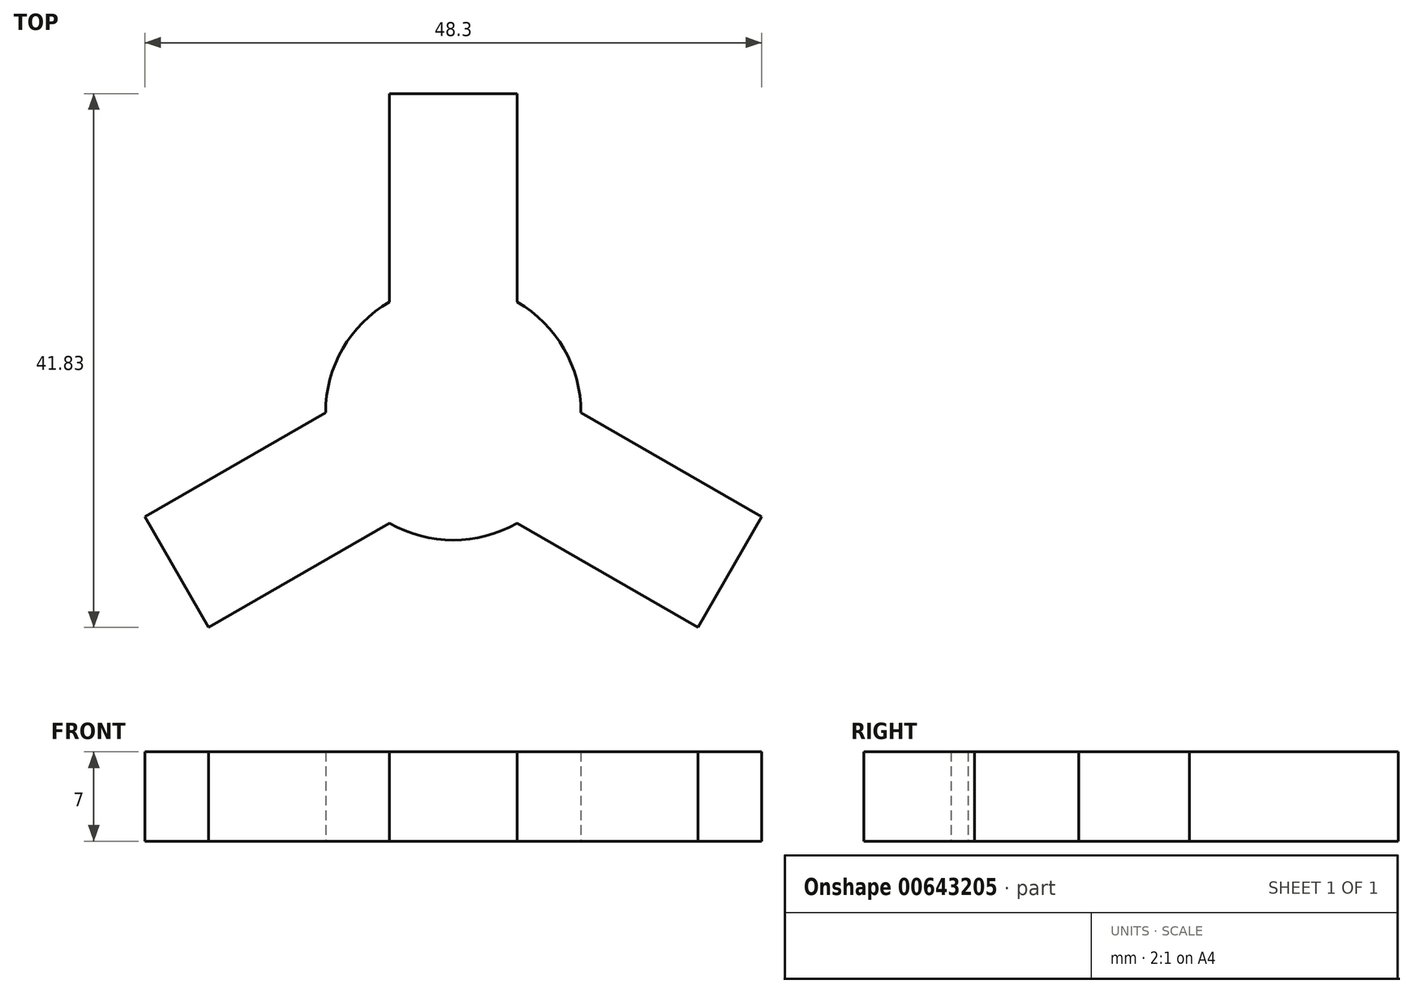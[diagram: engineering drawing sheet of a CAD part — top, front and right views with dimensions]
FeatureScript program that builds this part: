
annotation { "Feature Type Name" : "Feature", "Feature Type Description" : "" }
export const myFeature = defineFeature(function(context is Context, id is Id, definition is map)
    precondition{}
    {
        {
            var Q0;
            Q0=qCreatedBy(makeId("Top.planeOp"),FACE);
            var sketch = newSketch(context, id + "F0", { "sketchPlane" : qUnion([Q0])});
            skLineSegment(sketch, "E0", {"start": v(-25, 0) * mm, "end": v(25, 0) * mm, "construction": true});
            skLineSegment(sketch, "E1", {"start": v(0, -25) * mm, "end": v(0, 25) * mm, "construction": true});
            skLineSegment(sketch, "E2", {"start": v(-17.68, -17.68) * mm, "end": v(17.68, 17.68) * mm, "construction": true});
            skCircle(sketch, "E3", {"center": v(0, 0) * mm, "radius": 25 * mm, "construction": true});
            skLineSegment(sketch, "E4", {"start": v(17.68, -17.68) * mm, "end": v(-17.68, 17.68) * mm, "construction": true});
            skLineSegment(sketch, "E5", {"start": v(-21.65, -12.5) * mm, "end": v(21.65, 12.5) * mm, "construction": true});
            skLineSegment(sketch, "E6", {"start": v(-21.65, 12.5) * mm, "end": v(21.65, -12.5) * mm, "construction": true});
            skSolve(sketch);
        }
        {
            var Q0;
            Q0=qCreatedBy(makeId("Top.planeOp"),FACE);
            var sketch = newSketch(context, id + "F1", { "sketchPlane" : qUnion([Q0])});
            skLineSegment(sketch, "E7", {"start": v(-5, 0) * mm, "end": v(5, 0) * mm});
            skLineSegment(sketch, "E8", {"start": v(5, 0) * mm, "end": v(5, 5) * mm});
            skLineSegment(sketch, "E9", {"start": v(5, 25) * mm, "end": v(-5, 25) * mm});
            skLineSegment(sketch, "E10", {"start": v(-5, 25) * mm, "end": v(-5, 8.66) * mm});
            skCircle(sketch, "E11", {"center": v(0, 0) * mm, "radius": 10 * mm});
            skLineSegment(sketch, "E12", {"start": v(0, 0) * mm, "end": v(-5, 5) * mm});
            skLineSegment(sketch, "E13", {"start": v(0, 0) * mm, "end": v(5, 5) * mm});
            skLineSegment(sketch, "E14", {"start": v(-5, 5) * mm, "end": v(-5, 0) * mm});
            skLineSegment(sketch, "E15", {"start": v(5, 5) * mm, "end": v(5, 5) * mm});
            skLineSegment(sketch, "E16", {"start": v(5, 5) * mm, "end": v(5, 8.66) * mm});
            skLineSegment(sketch, "E17", {"start": v(-5, 8.66) * mm, "end": v(-5, 5) * mm});
            skLineSegment(sketch, "E18", {"start": v(5, 8.66) * mm, "end": v(5, 25) * mm});
            skLineSegment(sketch, "E19.1.0", {"start": v(-19.15, -16.83) * mm, "end": v(-5, -8.66) * mm});
            skLineSegment(sketch, "E19.1.1", {"start": v(-10, 0) * mm, "end": v(-24.15, -8.17) * mm});
            skLineSegment(sketch, "E19.1.2", {"start": v(-24.15, -8.17) * mm, "end": v(-19.15, -16.83) * mm});
            skLineSegment(sketch, "E19.2.0", {"start": v(24.15, -8.17) * mm, "end": v(10, 0) * mm});
            skLineSegment(sketch, "E19.2.1", {"start": v(5, -8.66) * mm, "end": v(19.15, -16.83) * mm});
            skLineSegment(sketch, "E19.2.2", {"start": v(19.15, -16.83) * mm, "end": v(24.15, -8.17) * mm});
            skSolve(sketch);
        }
        {
            var Q0;
            {var subQ10=sQuery(id+"F1.wireOp",EDGE,"E8");Q0=makeQuery(id+"F1.imprint","IMPRINT",FACE,{"disambiguationData":[TD([[makeQuery(id+"F1.imprint","IMPRINT",EDGE,{"derivedFrom":subQ10}),-1.0]])]});}
            var Q1;
            {var subQ0=sQuery(id+"F1.wireOp",EDGE,"E19.2.0");Q1=makeQuery(id+"F1.imprint","IMPRINT",FACE,{"disambiguationData":[TD([[makeQuery(id+"F1.imprint","IMPRINT",EDGE,{"derivedFrom":subQ0}),1.0]])]});}
            var Q2;
            {var subQ0=sQuery(id+"F1.wireOp",EDGE,"E8");Q2=makeQuery(id+"F1.imprint","IMPRINT",FACE,{"disambiguationData":[TD([[makeQuery(id+"F1.imprint","IMPRINT",EDGE,{"derivedFrom":subQ0}),1.0]])]});}
            var Q3;
            {var subQ2=sQuery(id+"F1.wireOp",EDGE,"E12");Q3=makeQuery(id+"F1.imprint","IMPRINT",FACE,{"disambiguationData":[TD([[makeQuery(id+"F1.imprint","IMPRINT",EDGE,{"derivedFrom":subQ2}),1.0]])]});}
            var Q4;
            Q4=makeQuery(id+"F1.imprint","IMPRINT",FACE,{"disambiguationData":[TD([[makeQuery(id+"F1.imprint","IMPRINT",EDGE,{"derivedFrom":sQuery(id+"F1.wireOp",EDGE,"E12")}),-1.0]])]});
            var Q5;
            Q5=makeQuery(id+"F1.imprint","IMPRINT",FACE,{"disambiguationData":[TD([[makeQuery(id+"F1.imprint","IMPRINT",EDGE,{"derivedFrom":sQuery(id+"F1.wireOp",EDGE,"E9")}),1.0]])]});
            var Q6;
            {var subQ0=sQuery(id+"F1.wireOp",EDGE,"E19.1.0");Q6=makeQuery(id+"F1.imprint","IMPRINT",FACE,{"disambiguationData":[TD([[makeQuery(id+"F1.imprint","IMPRINT",EDGE,{"derivedFrom":subQ0}),1.0]])]});}
            extrude(context, id + "F2", {"entities" : qUnion([Q0, Q1, Q2, Q3, Q4, Q5, Q6]), "depth" : 7 * mm, "offsetDistance" : 25 * mm});
        }
    });
